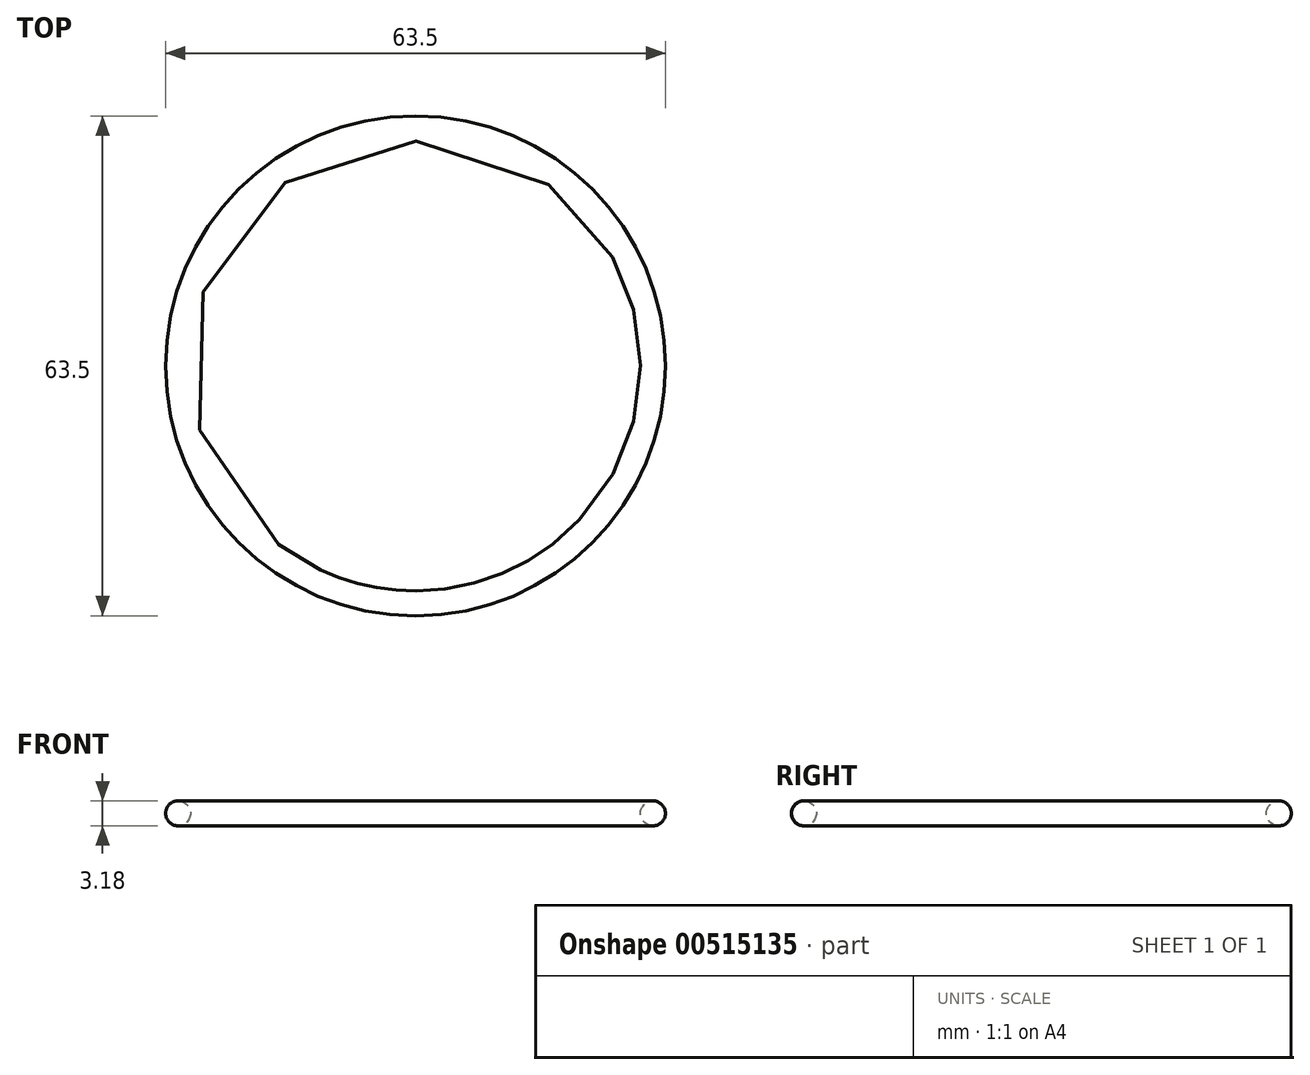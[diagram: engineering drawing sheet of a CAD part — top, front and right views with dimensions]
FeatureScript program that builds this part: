
annotation { "Feature Type Name" : "Feature", "Feature Type Description" : "" }
export const myFeature = defineFeature(function(context is Context, id is Id, definition is map)
    precondition{}
    {
        {
            var Q0;
            Q0=qCreatedBy(makeId("Right.planeOp"),FACE);
            var sketch = newSketch(context, id + "F0", { "sketchPlane" : qUnion([Q0])});
            skCircle(sketch, "E0", {"center": v(0, 0) * mm, "radius": 1.59 * mm});
            skSolve(sketch);
        }
        {
            var Q0;
            Q0=qCreatedBy(makeId("Top.planeOp"),FACE);
            var sketch = newSketch(context, id + "F1", { "sketchPlane" : qUnion([Q0])});
            skCircle(sketch, "E1", {"center": v(0.05, -30.16) * mm, "radius": 30.16 * mm});
            skPoint(sketch, "E1.first.point", {"position": v(0, 0) * mm});
            skPoint(sketch, "E1.second.point", {"position": v(0, -60.32) * mm});
            skPoint(sketch, "E1.third.point", {"position": v(-30.12, -30.08) * mm});
            skSolve(sketch);
        }
        {
            var Q0;
            Q0=makeQuery(id+"F0.imprint","IMPRINT",FACE,{"disambiguationData":[TD([[makeQuery(id+"F0.imprint","IMPRINT",EDGE,{"derivedFrom":sQuery(id+"F0.wireOp",EDGE,"E0")}),1.0]])]});
            var Q1;
            Q1=sQuery(id+"F1.wireOp",EDGE,"E1");
            sweep(context, id + "F2", {"profiles" : qUnion([Q0]), "path" : qUnion([Q1])});
        }
    });
